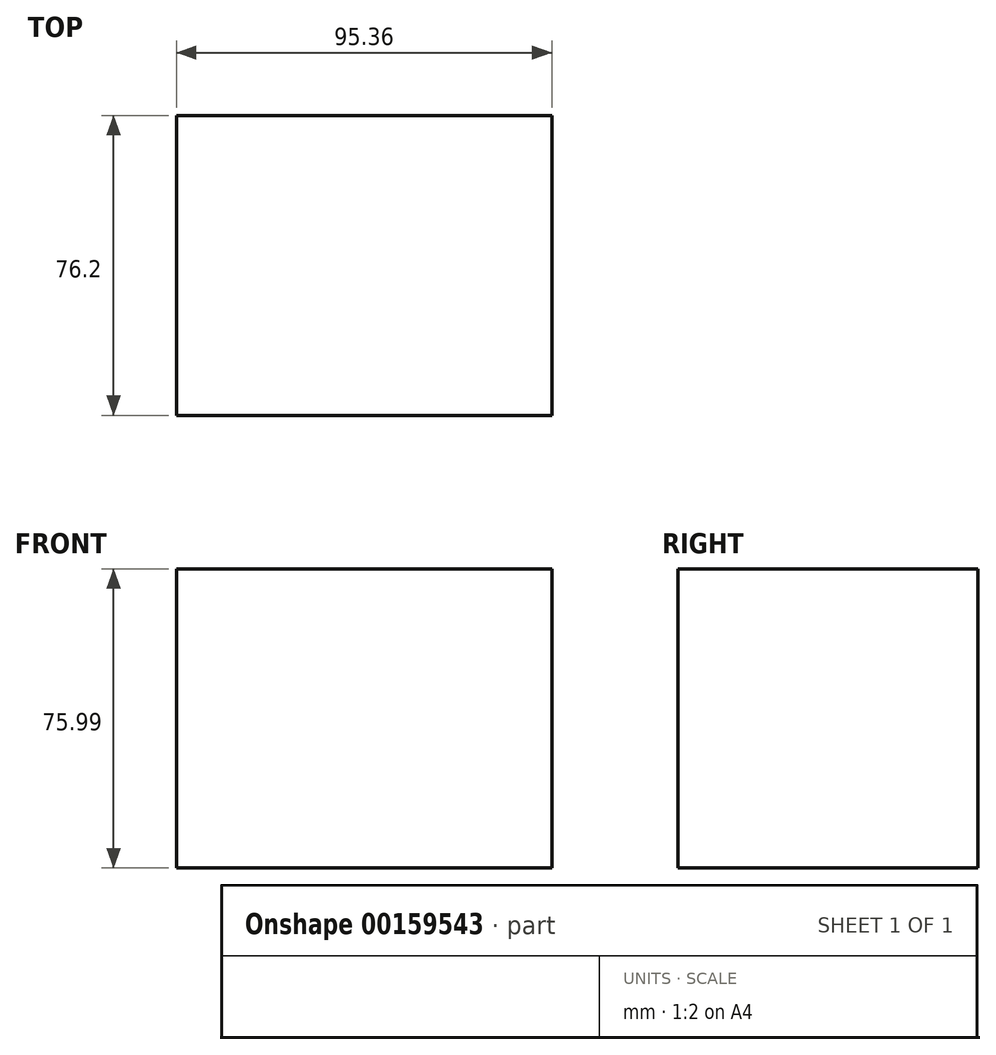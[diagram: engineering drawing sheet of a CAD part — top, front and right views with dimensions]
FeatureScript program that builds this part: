
annotation { "Feature Type Name" : "Feature", "Feature Type Description" : "" }
export const myFeature = defineFeature(function(context is Context, id is Id, definition is map)
    precondition{}
    {
        {
            var Q0;
            Q0=qCreatedBy(makeId("Front.planeOp"),FACE);
            var sketch = newSketch(context, id + "F0", { "sketchPlane" : qUnion([Q0])});
            skLineSegment(sketch, "E0.bottom", {"start": v(-47.83, 53.2) * mm, "end": v(47.53, 53.2) * mm});
            skLineSegment(sketch, "E0.top", {"start": v(-47.83, -22.8) * mm, "end": v(47.53, -22.8) * mm});
            skLineSegment(sketch, "E0.left", {"start": v(-47.83, 53.2) * mm, "end": v(-47.83, -22.8) * mm});
            skLineSegment(sketch, "E0.right", {"start": v(47.53, 53.2) * mm, "end": v(47.53, -22.8) * mm});
            skSolve(sketch);
        }
        {
            var Q0;
            Q0 = qSketchRegion(id + "F0", true);
            extrude(context, id + "F1", {"entities" : qUnion([Q0]), "depth" : 76.2 * mm});
        }
    });
